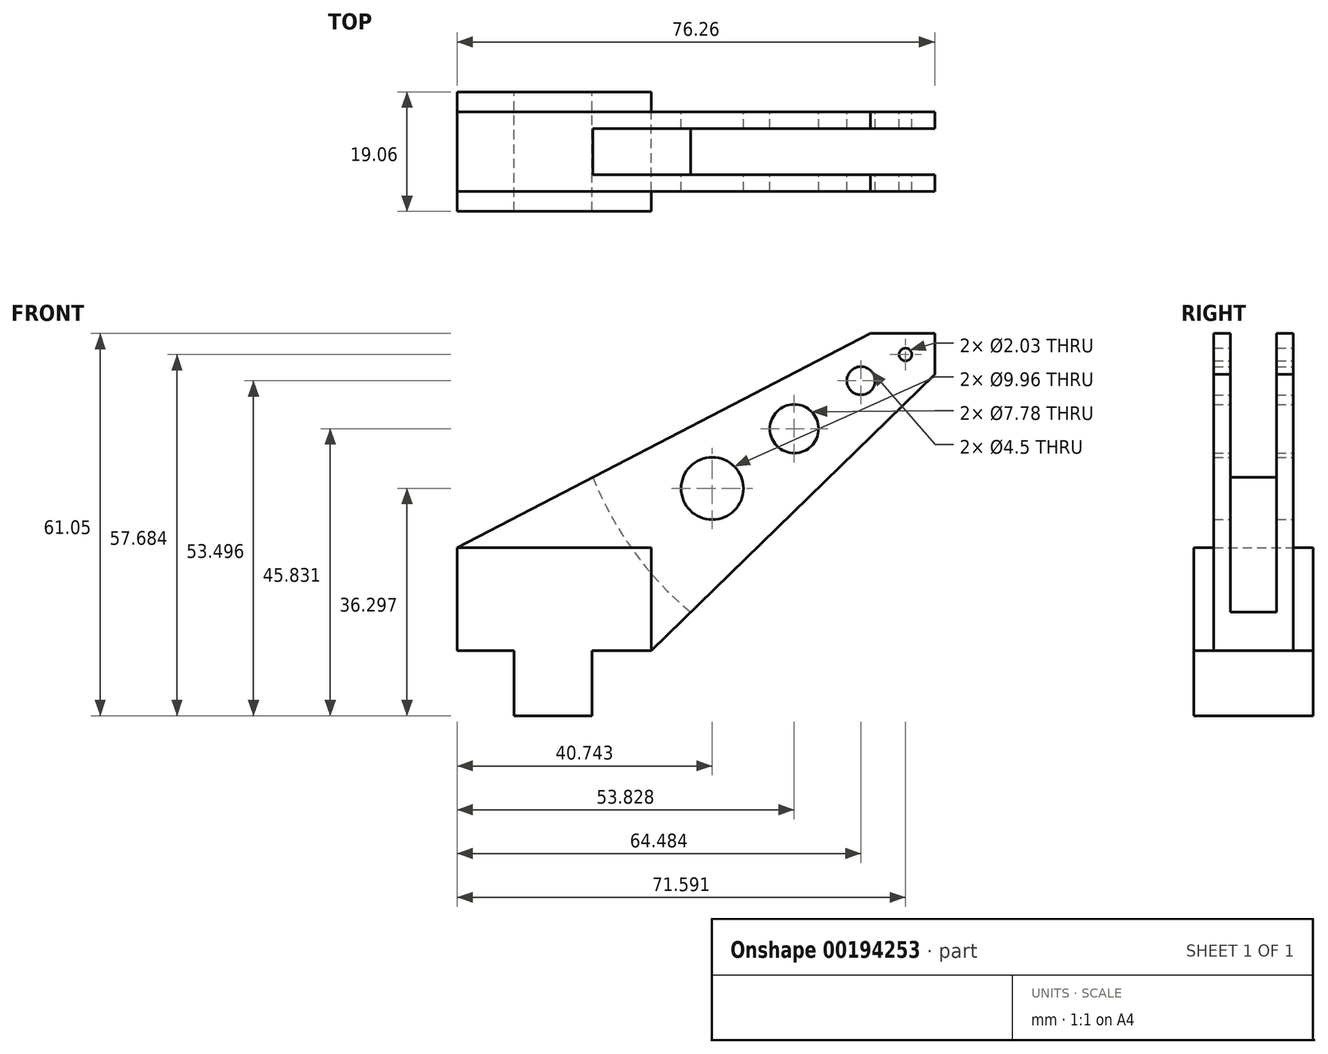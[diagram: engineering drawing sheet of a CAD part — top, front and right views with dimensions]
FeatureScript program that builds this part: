
annotation { "Feature Type Name" : "Feature", "Feature Type Description" : "" }
export const myFeature = defineFeature(function(context is Context, id is Id, definition is map)
    precondition{}
    {
        {
            var Q0;
            Q0=qCreatedBy(makeId("Front.planeOp"),FACE);
            var sketch = newSketch(context, id + "F0", { "sketchPlane" : qUnion([Q0])});
            skLineSegment(sketch, "E0.bottom", {"start": v(-6.13, 0) * mm, "end": v(6.32, 0) * mm});
            skLineSegment(sketch, "E0.top", {"start": v(-6.13, -10.4) * mm, "end": v(6.32, -10.4) * mm});
            skLineSegment(sketch, "E0.left", {"start": v(-6.13, 0) * mm, "end": v(-6.13, -10.4) * mm});
            skLineSegment(sketch, "E0.right", {"start": v(6.32, 0) * mm, "end": v(6.32, -10.4) * mm});
            skLineSegment(sketch, "E1.bottom", {"start": v(-15.22, 0) * mm, "end": v(15.8, 0) * mm});
            skLineSegment(sketch, "E1.top", {"start": v(-15.22, 16.46) * mm, "end": v(15.8, 16.46) * mm});
            skLineSegment(sketch, "E1.left", {"start": v(-15.22, 0) * mm, "end": v(-15.22, 16.46) * mm});
            skLineSegment(sketch, "E1.right", {"start": v(15.8, 0) * mm, "end": v(15.8, 16.46) * mm});
            skLineSegment(sketch, "E2", {"start": v(-15.22, 16.46) * mm, "end": v(50.77, 50.64) * mm});
            skLineSegment(sketch, "E3", {"start": v(15.8, 0) * mm, "end": v(61.04, 44.12) * mm});
            skLineSegment(sketch, "E4", {"start": v(61.04, 44.12) * mm, "end": v(61.04, 50.64) * mm});
            skLineSegment(sketch, "E5", {"start": v(61.04, 50.64) * mm, "end": v(50.77, 50.64) * mm});
            skCircle(sketch, "E6", {"center": v(56.37, 47.27) * mm, "radius": 1.02 * mm});
            skCircle(sketch, "E7", {"center": v(25.52, 25.89) * mm, "radius": 4.98 * mm});
            skCircle(sketch, "E8", {"center": v(38.6, 35.42) * mm, "radius": 3.89 * mm});
            skCircle(sketch, "E9", {"center": v(49.26, 43.09) * mm, "radius": 2.25 * mm});
            skSolve(sketch);
        }
        {
            var Q0;
            Q0=makeQuery(id+"F0.imprint","IMPRINT",FACE,{"disambiguationData":[TD([[makeQuery(id+"F0.imprint","IMPRINT",EDGE,{"derivedFrom":sQuery(id+"F0.wireOp",EDGE,"E0.top")}),1.0]])]});
            var Q1;
            Q1=makeQuery(id+"F0.imprint","IMPRINT",FACE,{"disambiguationData":[TD([[makeQuery(id+"F0.imprint","IMPRINT",EDGE,{"derivedFrom":sQuery(id+"F0.wireOp",EDGE,"E1.top")}),-1.0]])]});
            extrude(context, id + "F1", {"entities" : qUnion([Q0, Q1]), "endBound" : BoundingType.SYMMETRIC, "depth" : 19.05 * mm});
        }
        {
            var Q0;
            Q0=makeQuery(id+"F0.imprint","IMPRINT",FACE,{"disambiguationData":[TD([[makeQuery(id+"F0.imprint","IMPRINT",EDGE,{"derivedFrom":sQuery(id+"F0.wireOp",EDGE,"E1.top")}),1.0]])]});
            extrude(context, id + "F2", {"entities" : qUnion([Q0]), "operationType" : NewBodyOperationType.ADD, "endBound" : BoundingType.SYMMETRIC, "depth" : 12.7 * mm});
        }
        {
            var Q0;
            Q0=qCreatedBy(makeId("Front.planeOp"),FACE);
            var sketch = newSketch(context, id + "F3", { "sketchPlane" : qUnion([Q0])});
            skCircle(sketch, "E10", {"center": v(56.3, 47.29) * mm, "radius": 53.55 * mm});
            skSolve(sketch);
        }
        {
            var Q0;
            Q0=makeQuery(id+"F3.imprint","IMPRINT",FACE,{"disambiguationData":[TD([[makeQuery(id+"F3.imprint","IMPRINT",EDGE,{"derivedFrom":sQuery(id+"F3.wireOp",EDGE,"E10")}),1.0]])]});
            extrude(context, id + "F4", {"entities" : qUnion([Q0]), "operationType" : NewBodyOperationType.REMOVE, "endBound" : BoundingType.SYMMETRIC, "oppositeDirection" : true, "depth" : 7.37 * mm});
        }
    });
